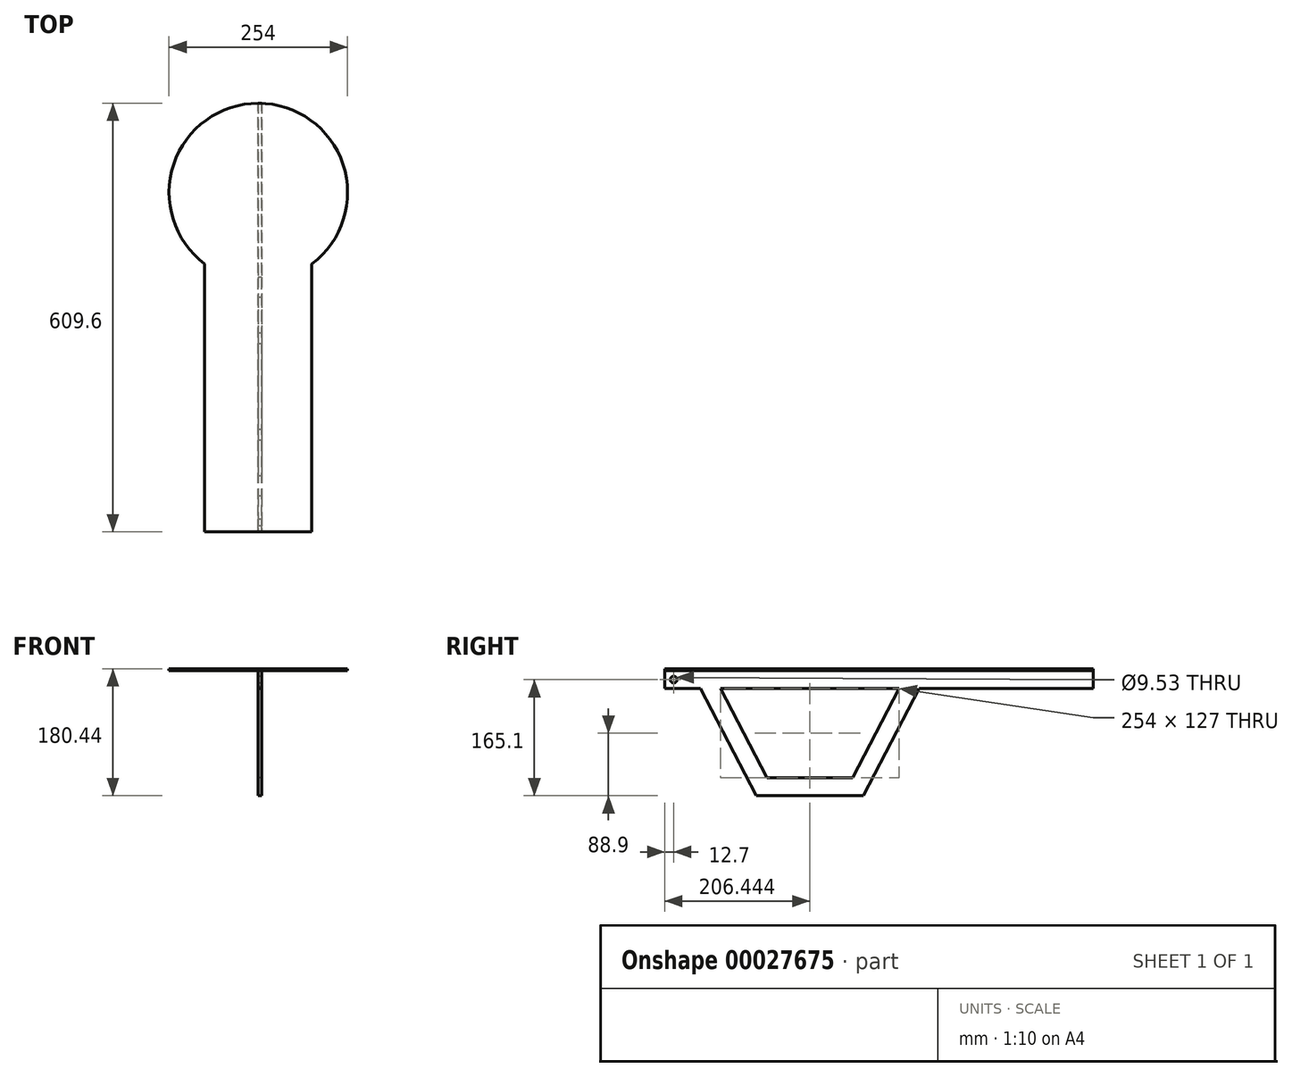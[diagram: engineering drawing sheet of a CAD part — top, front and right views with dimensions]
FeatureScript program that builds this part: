
annotation { "Feature Type Name" : "Feature", "Feature Type Description" : "" }
export const myFeature = defineFeature(function(context is Context, id is Id, definition is map)
    precondition{}
    {
        {
            var Q0;
            Q0=qCreatedBy(makeId("Right.planeOp"),FACE);
            var sketch = newSketch(context, id + "F0", { "sketchPlane" : qUnion([Q0])});
            skLineSegment(sketch, "E0", {"start": v(-609.6, 25.4) * mm, "end": v(0, 25.4) * mm});
            skLineSegment(sketch, "E1", {"start": v(0, 25.4) * mm, "end": v(0, 0) * mm});
            skLineSegment(sketch, "E2", {"start": v(0, 0) * mm, "end": v(-247.51, 0) * mm});
            skLineSegment(sketch, "E3", {"start": v(-609.6, 0) * mm, "end": v(-609.6, 25.4) * mm});
            skLineSegment(sketch, "E4", {"start": v(-247.51, 0) * mm, "end": v(-326.96, -152.4) * mm});
            skLineSegment(sketch, "E5", {"start": v(-326.96, -152.4) * mm, "end": v(-479.36, -152.4) * mm});
            skLineSegment(sketch, "E6", {"start": v(-479.36, -152.4) * mm, "end": v(-558.8, 0) * mm});
            skLineSegment(sketch, "E7.0", {"start": v(-463.95, -127) * mm, "end": v(-530.16, 0) * mm});
            skLineSegment(sketch, "E7.1", {"start": v(-342.36, -127) * mm, "end": v(-463.95, -127) * mm});
            skLineSegment(sketch, "E7.2", {"start": v(-276.16, 0) * mm, "end": v(-342.36, -127) * mm});
            skLineSegment(sketch, "E8.trimOffspring", {"start": v(-558.8, 0) * mm, "end": v(-609.6, 0) * mm});
            skLineSegment(sketch, "E9.trimOffspring", {"start": v(-276.16, 0) * mm, "end": v(-530.16, 0) * mm});
            skCircle(sketch, "E10", {"center": v(-596.9, 12.7) * mm, "radius": 4.76 * mm});
            skSolve(sketch);
        }
        {
            var Q0;
            Q0 = qSketchRegion(id + "F0", true);
            extrude(context, id + "F1", {"entities" : qUnion([Q0]), "depth" : 4.76 * mm});
        }
        {
            var Q0;
            Q0=makeQuery(id+"F1.opExtrude","CAP_FACE",FACE,{"disambiguationData":[OSD([sQuery(id+"F0.wireOp",EDGE,"E0"),sQuery(id+"F0.wireOp",EDGE,"E1"),sQuery(id+"F0.wireOp",EDGE,"E2"),sQuery(id+"F0.wireOp",EDGE,"E3"),sQuery(id+"F0.wireOp",EDGE,"E4"),sQuery(id+"F0.wireOp",EDGE,"E5"),sQuery(id+"F0.wireOp",EDGE,"E6"),sQuery(id+"F0.wireOp",EDGE,"E7.0"),sQuery(id+"F0.wireOp",EDGE,"E7.1"),sQuery(id+"F0.wireOp",EDGE,"E7.2"),sQuery(id+"F0.wireOp",EDGE,"E8.trimOffspring"),sQuery(id+"F0.wireOp",EDGE,"E9.trimOffspring"),sQuery(id+"F0.wireOp",EDGE,"E10")])],"isStart":false});
            var sketch = newSketch(context, id + "F2", { "sketchPlane" : qUnion([Q0])});
            skLineSegment(sketch, "E11.bottom", {"start": v(-609.6, 25.4) * mm, "end": v(0, 25.4) * mm});
            skLineSegment(sketch, "E11.top", {"start": v(-609.6, 28.04) * mm, "end": v(0, 28.04) * mm});
            skLineSegment(sketch, "E11.left", {"start": v(-609.6, 25.4) * mm, "end": v(-609.6, 28.04) * mm});
            skLineSegment(sketch, "E11.right", {"start": v(0, 25.4) * mm, "end": v(0, 28.04) * mm});
            skSolve(sketch);
        }
        {
            var Q0;
            Q0 = qSketchRegion(id + "F2", true);
            extrude(context, id + "F3", {"entities" : qUnion([Q0]), "depth" : 152.4 * mm, "hasSecondDirection" : true, "secondDirectionOppositeDirection" : true, "secondDirectionDepth" : 152.4 * mm});
        }
        {
            var Q0;
            Q0=makeQuery(id+"F3.opExtrude","SWEPT_FACE",FACE,{"disambiguationData":[OSD([sQuery(id+"F2.wireOp",EDGE,"E11.top")])]});
            var sketch = newSketch(context, id + "F4", { "sketchPlane" : qUnion([Q0])});
            skLineSegment(sketch, "E12", {"start": v(0, -609.6) * mm, "end": v(0, 0) * mm, "construction": true});
            skArc(sketch, "E13", {"start": v(76.2, -228.6) * mm, "mid": v(0, 0) * mm, "end": v(-76.2, -228.6) * mm});
            skLineSegment(sketch, "E14", {"start": v(76.2, -609.6) * mm, "end": v(76.2, -228.6) * mm});
            skLineSegment(sketch, "E15.MirrorCS", {"start": v(152.4, -609.6) * mm, "end": v(152.4, 0) * mm, "construction": true});
            skLineSegment(sketch, "E16.MirrorCS", {"start": v(-76.2, -609.6) * mm, "end": v(-76.2, -228.6) * mm});
            skLineSegment(sketch, "E17", {"start": v(-76.2, -609.6) * mm, "end": v(76.2, -609.6) * mm});
            skCircle(sketch, "E18", {"center": v(0, -272.84) * mm, "radius": 876.1 * mm});
            skSolve(sketch);
        }
        {
            var Q0;
            Q0 = qSketchRegion(id + "F4", true);
            extrude(context, id + "F5", {"entities" : qUnion([Q0]), "operationType" : NewBodyOperationType.REMOVE, "oppositeDirection" : true, "depth" : 25.4 * mm});
        }
    });
